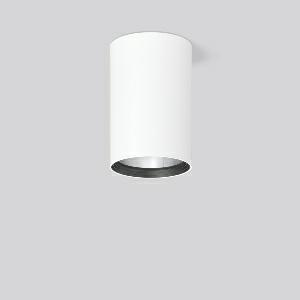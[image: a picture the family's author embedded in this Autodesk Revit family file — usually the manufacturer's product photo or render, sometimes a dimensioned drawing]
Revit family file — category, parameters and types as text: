
# Revit family: heledon_maxi_a_931226_002_79ec
name_source: partatom
category: Lighting Fixtures
units: mm (PartAtom-declared; Revit-internal decimal feet)

## family parameters
Cut with Voids When Loaded = No
Host = Face
Light Source = No
Part Type = Normal
Room Calculation Point = No
Round Connector Dimension = Use Diameter
Shared = No

## types (1)
- HELEDON maxi A (1 x LED Modul 930, 4150 lm, 3000)
    Apparent Load = 35 VA
    Approval mark = CE
    CIE Flux Codes = 97 100 100 100 100
    Color Rendering = 90
    Color Temperature = 3000
    Default Elevation = 1800 mm
    Description = Series: HELEDON maxi
Cylindrical surface-mounted downlight. Housing: die-cast aluminium, powder-coated. Internal ceiling frame polycarbonate with bayonet mounting. Black plastic ring and recessed LED to prevent glare from the side. Optical assembly with reflector made of MIRO-Silver with 98% total light reflection for outstanding efficiency - can be changed without tools. Best colour rendering index Ra>90. Suitable for Ceiling mounting. Easy installation with a separate ceiling frame with bayonet mounting and plug connection. Driver integrated. Connected via plug-in connector. High quality converter without flickering and stroboscopic effect. The following accessories can be mounted without use of tools: interchangeable lenses, decorative glasses, honeycomb louvre, clear and frosted diffusers, white interchangeable plastic ring. 
Colour: traffic white, matt (RAL 9016)
Diameter: 123 mm
Height: 183 mm
Lamp: LED
Socket: without socket
Colour temperature: 3000K
Colour rendering index (CRI): 92
System power: 35 W
Rated luminous flux: 4150 lm
Luminous efficiency: 119 lm/W
Control gear: Regulated power supply
Protection class: I
Type of protection: IP 20
    Height = 183 mm
    Lamp = 1 x LED Modul 930
    Lamp Light Flux = 4150 lm
    Lamp count = 1
    Length = 123 mm
    Lifetime = 50000 h
    Luminous efficacy = 119 lm/W
    Manufacturer = RZB
    ModVariant = No
    Model = 931226.002
    Mounting Place = Ceiling
    Mounting Type = Surface mounted
    Number of Poles = 1
    OnlyDefault = Yes
    Power Factor = 1
    Product Name = HELEDON maxi A
    Product group = Surface mounted downlights
    ProductGroupID = 302
    Protection Class = Protection class I
    Protection Degree = IP 20
    RLX_Detail_Level = 1
    RLX_Emergency_Light_Flux = 0 lm
    RLX_Emergency_Type = 0
    RLX_Emergency_Type_DB = No
    RlxData = <blob elided: 95949 chars, md5=a0f98de3>
    Socket = socket
    Standby Power = 0 W
    System Light Flux = 4150 lm
    System Power = 35 W
    Type Comments = Product without accessories
    Type Image = 931192.002.jpg
    URL = http://relux.com
    VarID = ---
    Voltage = 230 V
    Voltage Range = 220-240 V
    Weight = 0.00 kg
    Width = 0 mm  [stored 0 ft]

note: [stored X ft] marks values corroborated as IEEE doubles in the binary element streams (Revit-internal decimal feet)

## geometry (parser evidence)
native form markers: Blend x4, Sweep x11
no freeform markers — native parametric forms only
